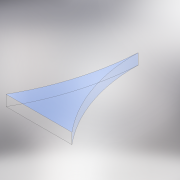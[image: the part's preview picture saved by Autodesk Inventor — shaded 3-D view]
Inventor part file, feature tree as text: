
AUTODESK INVENTOR PART (.ipt)
format: ipt  version: 2020 (Build 240168000, 168)  size: 122,368 bytes
history: native  units: in
note: dims shown in document units (in); Inventor stores cm internally (conversion verified against a paired STEP export)
features: extrude x1, sketch x1
ambient origin geometry x8: Origin, YZ Plane, XZ Plane, XY Plane, X Axis, Y Axis, Z Axis, Center Point
bodies: Body1 (feature_tree)
feature tree (2):
  extrude  "Extrusion2"  [1 undecoded]
  sketch  "Sketch1"  dims[d2=0.0197in d3=0.0in]
note: 1 required parameter value undecoded (feature->parameter linkage not recoverable at this tier; creation-order binding heuristic only, values carry confidence <= 0.55)
